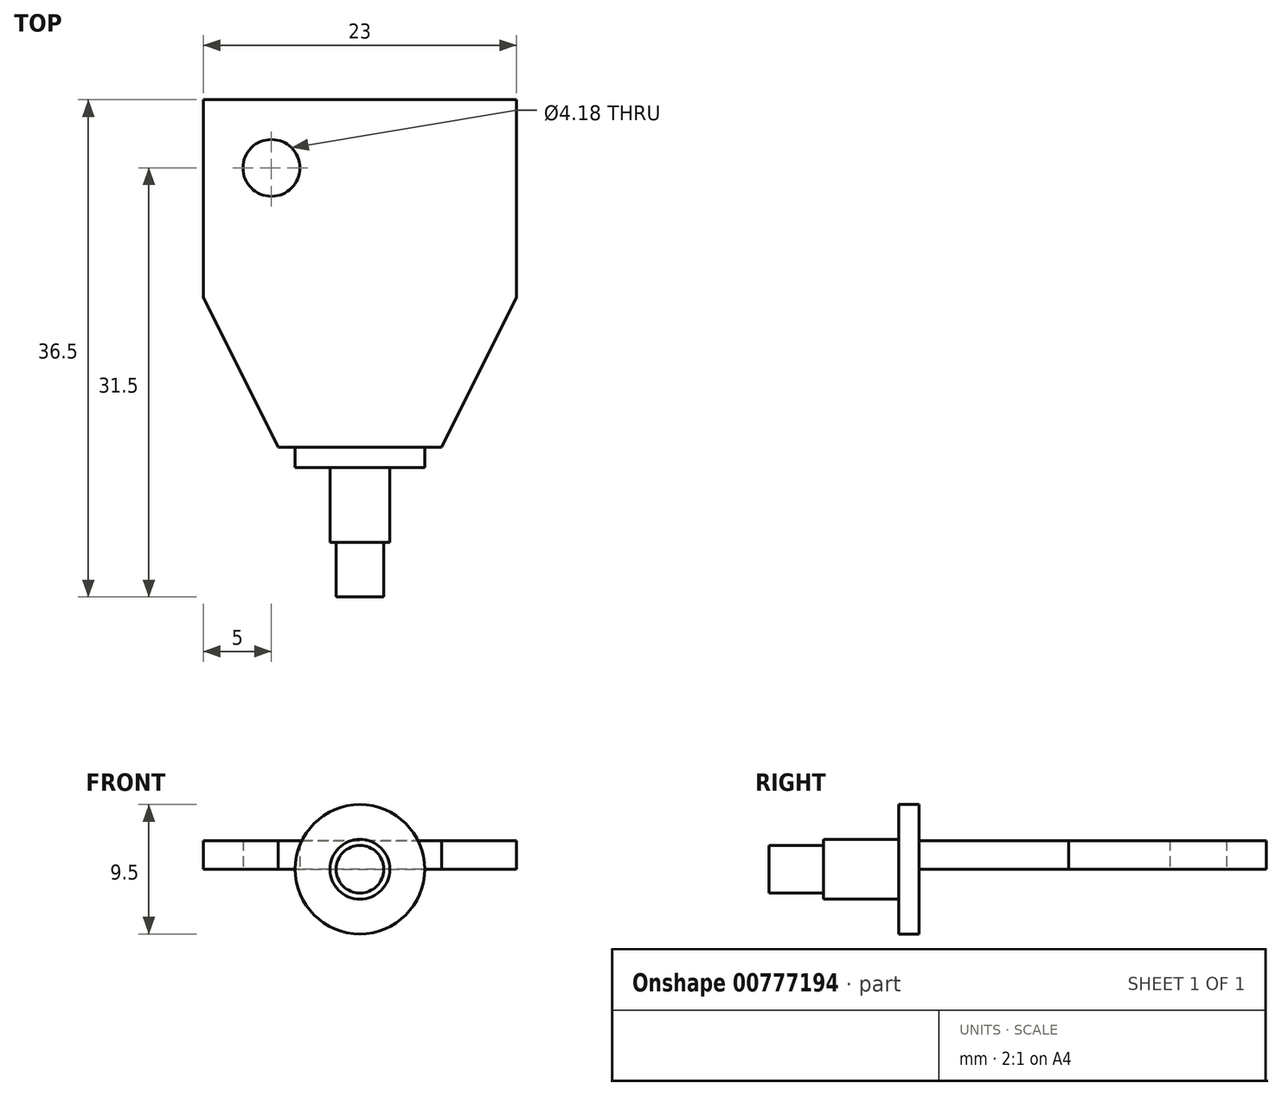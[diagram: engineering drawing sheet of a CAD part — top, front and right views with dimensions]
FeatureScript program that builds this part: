
annotation { "Feature Type Name" : "Feature", "Feature Type Description" : "" }
export const myFeature = defineFeature(function(context is Context, id is Id, definition is map)
    precondition{}
    {
        {
            var Q0;
            Q0=qCreatedBy(makeId("Top.planeOp"),FACE);
            var sketch = newSketch(context, id + "F0", { "sketchPlane" : qUnion([Q0])});
            skLineSegment(sketch, "E0", {"start": v(-6, 0) * mm, "end": v(6, 0) * mm});
            skLineSegment(sketch, "E1", {"start": v(6, 0) * mm, "end": v(11.5, 11) * mm});
            skLineSegment(sketch, "E2", {"start": v(11.5, 11) * mm, "end": v(11.5, 25.5) * mm});
            skLineSegment(sketch, "E3", {"start": v(11.5, 25.5) * mm, "end": v(-11.5, 25.5) * mm});
            skLineSegment(sketch, "E4", {"start": v(-11.5, 25.5) * mm, "end": v(-11.5, 11) * mm});
            skLineSegment(sketch, "E5", {"start": v(-11.5, 11) * mm, "end": v(-6, 0) * mm});
            skCircle(sketch, "E6", {"center": v(-6.5, 20.5) * mm, "radius": 2.09 * mm});
            skSolve(sketch);
        }
        {
            var Q0;
            Q0=makeQuery(id+"F0.imprint","IMPRINT",FACE,{"disambiguationData":[TD([[makeQuery(id+"F0.imprint","IMPRINT",EDGE,{"derivedFrom":sQuery(id+"F0.wireOp",EDGE,"E0")}),1.0]])]});
            extrude(context, id + "F1", {"entities" : qUnion([Q0]), "depth" : 2.1 * mm, "offsetDistance" : 25 * mm});
        }
        {
            var Q0;
            Q0=qCreatedBy(makeId("Top.planeOp"),FACE);
            var sketch = newSketch(context, id + "F2", { "sketchPlane" : qUnion([Q0])});
            skLineSegment(sketch, "E7", {"start": v(0, 0) * mm, "end": v(0, -11) * mm});
            skLineSegment(sketch, "E8", {"start": v(0, -11) * mm, "end": v(1.75, -11) * mm});
            skLineSegment(sketch, "E9", {"start": v(1.75, -11) * mm, "end": v(1.75, -7) * mm});
            skLineSegment(sketch, "E10", {"start": v(1.75, -7) * mm, "end": v(2.2, -7) * mm});
            skLineSegment(sketch, "E11", {"start": v(2.2, -7) * mm, "end": v(2.2, -1.5) * mm});
            skLineSegment(sketch, "E12", {"start": v(2.2, -1.5) * mm, "end": v(4.75, -1.5) * mm});
            skLineSegment(sketch, "E13", {"start": v(4.75, -1.5) * mm, "end": v(4.75, 0) * mm});
            skLineSegment(sketch, "E14", {"start": v(4.75, 0) * mm, "end": v(0, 0) * mm});
            skLineSegment(sketch, "E15", {"start": v(0, 29.01) * mm, "end": v(0, -31.49) * mm, "construction": true});
            skSolve(sketch);
        }
        {
            var Q0;
            Q0=makeQuery(id+"F2.imprint","IMPRINT",FACE,{"disambiguationData":[TD([[makeQuery(id+"F2.imprint","IMPRINT",EDGE,{"derivedFrom":sQuery(id+"F2.wireOp",EDGE,"E7")}),1.0]])]});
            var Q1;
            Q1=sQuery(id+"F2.wireOp",EDGE,"E15");
            revolve(context, id + "F3", {"operationType" : NewBodyOperationType.ADD, "surfaceOperationType" : NewSurfaceOperationType.NEW, "entities" : qUnion([Q0]), "axis" : qUnion([Q1]), "revolveType" : RevolveType.FULL});
        }
    });
